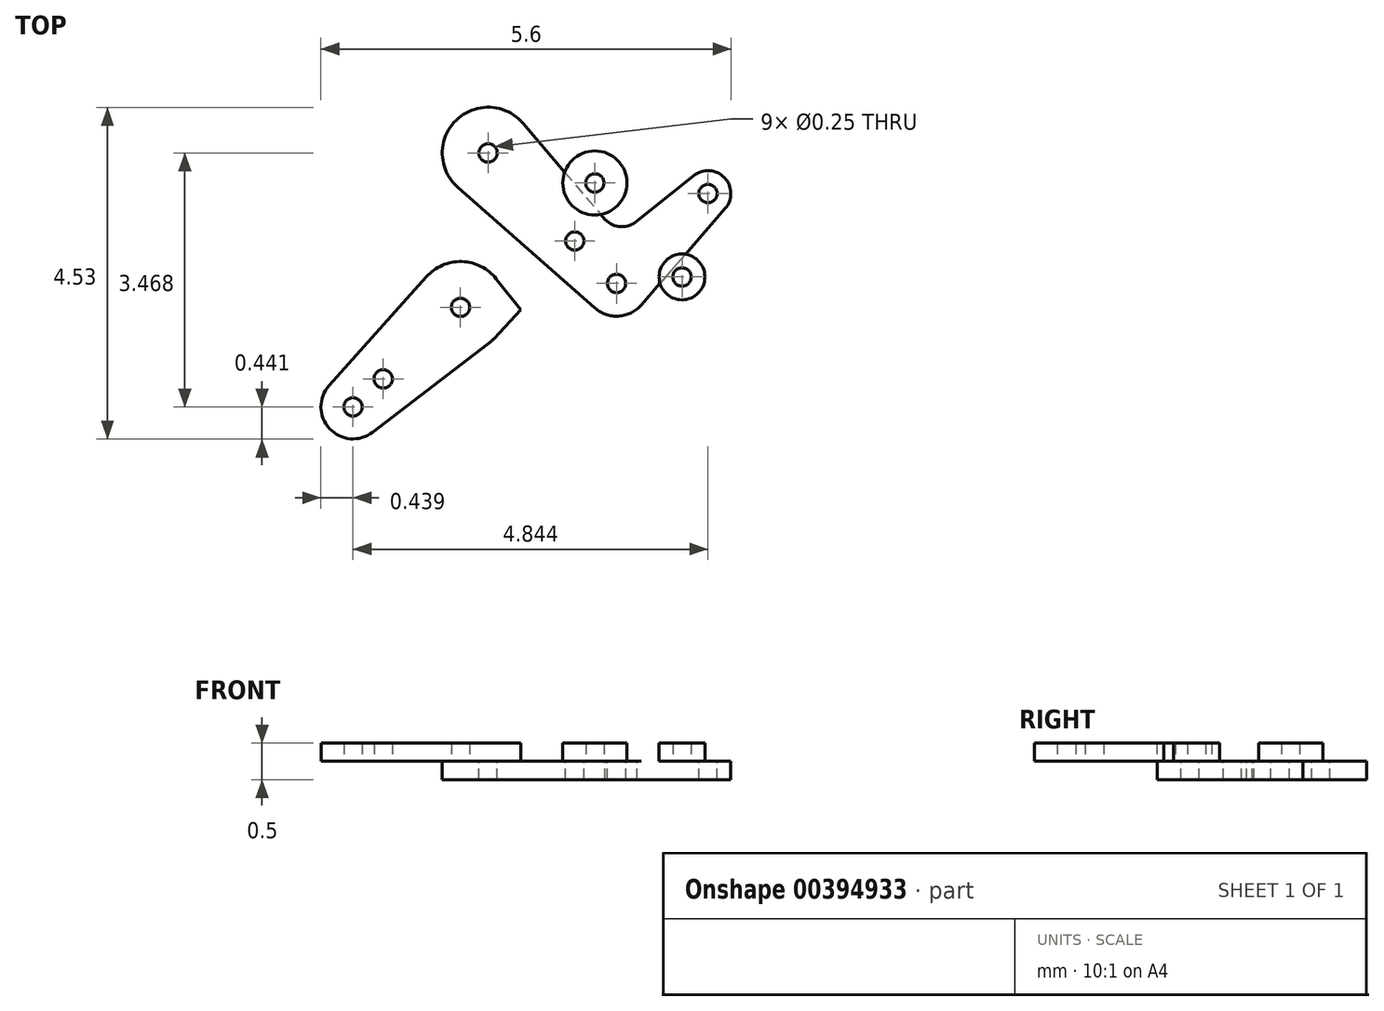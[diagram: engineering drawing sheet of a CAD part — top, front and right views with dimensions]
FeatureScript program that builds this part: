
annotation { "Feature Type Name" : "Feature", "Feature Type Description" : "" }
export const myFeature = defineFeature(function(context is Context, id is Id, definition is map)
    precondition{}
    {
        {
            var Q0;
            Q0=qCreatedBy(makeId("Top.planeOp"),FACE);
            var sketch = newSketch(context, id + "F0", { "sketchPlane" : qUnion([Q0])});
            skLineSegment(sketch, "E0", {"start": v(0, 0) * mm, "end": v(-3.3, -3.06) * mm, "construction": true});
            skLineSegment(sketch, "E1", {"start": v(0, 0) * mm, "end": v(1.19, -1.28) * mm, "construction": true});
            skLineSegment(sketch, "E2", {"start": v(-1.83, -1.7) * mm, "end": v(-0.13, -3.53) * mm, "construction": true});
            skLineSegment(sketch, "E3", {"start": v(-0.13, -3.53) * mm, "end": v(1.15, -2.34) * mm, "construction": true});
            skCircle(sketch, "E4", {"center": v(-3.3, -3.06) * mm, "radius": 0.44 * mm});
            skCircle(sketch, "E5", {"center": v(-1.83, -1.7) * mm, "radius": 0.63 * mm});
            skCircle(sketch, "E6", {"center": v(0, 0) * mm, "radius": 0.44 * mm});
            skCircle(sketch, "E7", {"center": v(1.15, -2.34) * mm, "radius": 0.31 * mm});
            skLineSegment(sketch, "E8", {"start": v(-3.63, -2.77) * mm, "end": v(-2.3, -1.28) * mm});
            skLineSegment(sketch, "E9", {"start": v(-2.22, -1.21) * mm, "end": v(-0.27, 0.34) * mm});
            skLineSegment(sketch, "E10", {"start": v(-1.45, -2.2) * mm, "end": v(-3.03, -3.4) * mm});
            skLineSegment(sketch, "E11", {"start": v(1.43, -1.08) * mm, "end": v(0.34, 0.27) * mm});
            skLineSegment(sketch, "E12", {"start": v(0.21, -3.8) * mm, "end": v(1.38, -2.56) * mm});
            skCircle(sketch, "E13", {"center": v(-0.13, -3.53) * mm, "radius": 0.12 * mm});
            skCircle(sketch, "E14", {"center": v(1.15, -2.34) * mm, "radius": 0.12 * mm});
            skCircle(sketch, "E15", {"center": v(1.19, -1.28) * mm, "radius": 0.12 * mm});
            skCircle(sketch, "E16", {"center": v(0, 0) * mm, "radius": 0.12 * mm});
            skCircle(sketch, "E17", {"center": v(-3.3, -3.06) * mm, "radius": 0.12 * mm});
            skCircle(sketch, "E18", {"center": v(-1.83, -1.7) * mm, "radius": 0.12 * mm});
            skLineSegment(sketch, "E19.trimOffspring", {"start": v(-0.24, -0.9) * mm, "end": v(-1.38, -2.12) * mm});
            skPoint(sketch, "E20.visualSharp", {"position": v(0.02, -0.62) * mm});
            skArc(sketch, "E20.filletArc", {"start": v(0.2, -0.88) * mm, "mid": v(-0.02, -0.8) * mm, "end": v(-0.24, -0.9) * mm});
            skCircle(sketch, "E21", {"center": v(-0.13, -3.53) * mm, "radius": 0.44 * mm});
            skCircle(sketch, "E22", {"center": v(1.19, -1.28) * mm, "radius": 0.31 * mm});
            skCircle(sketch, "E23", {"center": v(-0.69, -2.94) * mm, "radius": 0.12 * mm});
            skCircle(sketch, "E24", {"center": v(-2.89, -2.68) * mm, "radius": 0.12 * mm});
            skLineSegment(sketch, "E25", {"start": v(-1.34, -1.3) * mm, "end": v(-0.26, -2.67) * mm});
            skLineSegment(sketch, "E26", {"start": v(0.95, -2.1) * mm, "end": v(0.18, -2.72) * mm});
            skLineSegment(sketch, "E27.trimOffspring", {"start": v(0.19, -3.23) * mm, "end": v(0.2, -3.26) * mm});
            skPoint(sketch, "E28.visualSharp", {"position": v(-0.07, -2.92) * mm});
            skArc(sketch, "E28.filletArc", {"start": v(-0.26, -2.67) * mm, "mid": v(-0.05, -2.79) * mm, "end": v(0.18, -2.72) * mm});
            skLineSegment(sketch, "E29", {"start": v(0.2, -0.88) * mm, "end": v(1, -1.53) * mm});
            skLineSegment(sketch, "E30", {"start": v(-2.26, -2.16) * mm, "end": v(-0.43, -3.85) * mm});
            skSolve(sketch);
        }
        {
            var Q0;
            {var subQ0=sQuery(id+"F0.wireOp",EDGE,"E8");Q0=makeQuery(id+"F0.imprint","IMPRINT",FACE,{"disambiguationData":[TD([[makeQuery(id+"F0.imprint","IMPRINT",EDGE,{"derivedFrom":subQ0}),-1.0]])]});}
            var Q1;
            Q1=makeQuery(id+"F0.imprint","IMPRINT",FACE,{"disambiguationData":[TD([[makeQuery(id+"F0.imprint","IMPRINT",EDGE,{"derivedFrom":sQuery(id+"F0.wireOp",EDGE,"E17")}),-1.0]])]});
            var Q2;
            {var subQ1=sQuery(id+"F0.wireOp",EDGE,"E9");Q2=makeQuery(id+"F0.imprint","IMPRINT",FACE,{"disambiguationData":[TD([[makeQuery(id+"F0.imprint","IMPRINT",EDGE,{"derivedFrom":subQ1}),-1.0]])]});}
            var Q3;
            {var subQ0=sQuery(id+"F0.wireOp",EDGE,"E19.trimOffspring");var subQ1=sQuery(id+"F0.wireOp",EDGE,"E5");var subQ2=makeQuery(id+"F0.imprint","INTERSECT",VERTEX,{"derivedFrom":[subQ1,subQ0]});Q3=makeQuery(id+"F0.imprint","IMPRINT",FACE,{"disambiguationData":[TD([[makeQuery(id+"F0.imprint","IMPRINT",EDGE,{"disambiguationData":[TD([[subQ2,-1.0]])],"derivedFrom":subQ1}),-1.0]])]});}
            var Q4;
            {var subQ0=sQuery(id+"F0.wireOp",EDGE,"E10");var subQ1=sQuery(id+"F0.wireOp",EDGE,"E5");var subQ2=makeQuery(id+"F0.imprint","INTERSECT",VERTEX,{"derivedFrom":[subQ1,subQ0]});Q4=makeQuery(id+"F0.imprint","IMPRINT",FACE,{"disambiguationData":[TD([[makeQuery(id+"F0.imprint","IMPRINT",EDGE,{"disambiguationData":[TD([[subQ2,1.0]])],"derivedFrom":subQ1}),-1.0]])]});}
            var Q5;
            Q5=makeQuery(id+"F0.imprint","IMPRINT",FACE,{"disambiguationData":[TD([[makeQuery(id+"F0.imprint","IMPRINT",EDGE,{"derivedFrom":sQuery(id+"F0.wireOp",EDGE,"E15")}),-1.0]])]});
            var Q6;
            Q6=makeQuery(id+"F0.imprint","IMPRINT",FACE,{"disambiguationData":[TD([[makeQuery(id+"F0.imprint","IMPRINT",EDGE,{"derivedFrom":sQuery(id+"F0.wireOp",EDGE,"E16")}),-1.0]])]});
            var Q7;
            Q7=makeQuery(id+"F0.imprint","IMPRINT",FACE,{"disambiguationData":[TD([[makeQuery(id+"F0.imprint","IMPRINT",EDGE,{"derivedFrom":sQuery(id+"F0.wireOp",EDGE,"E18")}),-1.0]])]});
            extrude(context, id + "F1", {"entities" : qUnion([Q0, Q1, Q2, Q3, Q4, Q5, Q6, Q7]), "depth" : .25 * mm});
        }
        {
            var Q0;
            Q0=qCreatedBy(makeId("Top.planeOp"),FACE);
            var sketch = newSketch(context, id + "F2", { "sketchPlane" : qUnion([Q0])});
            skLineSegment(sketch, "E31", {"start": v(-1.46, 0.4) * mm, "end": v(0.3, -1.37) * mm, "construction": true});
            skLineSegment(sketch, "E32", {"start": v(0.3, -1.37) * mm, "end": v(1.54, -0.14) * mm, "construction": true});
            skCircle(sketch, "E33", {"center": v(-1.46, 0.4) * mm, "radius": 0.63 * mm});
            skCircle(sketch, "E34", {"center": v(1.54, -0.14) * mm, "radius": 0.31 * mm});
            skCircle(sketch, "E35", {"center": v(0.3, -1.37) * mm, "radius": 0.12 * mm});
            skCircle(sketch, "E36", {"center": v(1.54, -0.14) * mm, "radius": 0.12 * mm});
            skCircle(sketch, "E37", {"center": v(-1.46, 0.4) * mm, "radius": 0.12 * mm});
            skCircle(sketch, "E38", {"center": v(0.3, -1.37) * mm, "radius": 0.45 * mm});
            skCircle(sketch, "E39", {"center": v(-0.27, -0.8) * mm, "radius": 0.12 * mm});
            skArc(sketch, "E40.filletArc", {"start": v(0.14, -0.5) * mm, "mid": v(0.35, -0.6) * mm, "end": v(0.57, -0.52) * mm});
            skLineSegment(sketch, "E41", {"start": v(-1.87, -0.06) * mm, "end": v(0, -1.7) * mm});
            skLineSegment(sketch, "E42", {"start": v(-0.98, 0.82) * mm, "end": v(0.14, -0.5) * mm});
            skLineSegment(sketch, "E43", {"start": v(0.57, -0.52) * mm, "end": v(1.35, 0.1) * mm});
            skLineSegment(sketch, "E44", {"start": v(1.78, -0.35) * mm, "end": v(0.63, -1.67) * mm});
            skSolve(sketch);
        }
        {
            var Q0;
            Q0 = qSketchRegion(id + "F2", true);
            extrude(context, id + "F3", {"entities" : qUnion([Q0]), "oppositeDirection" : true, "depth" : .25 * mm});
        }
    });
